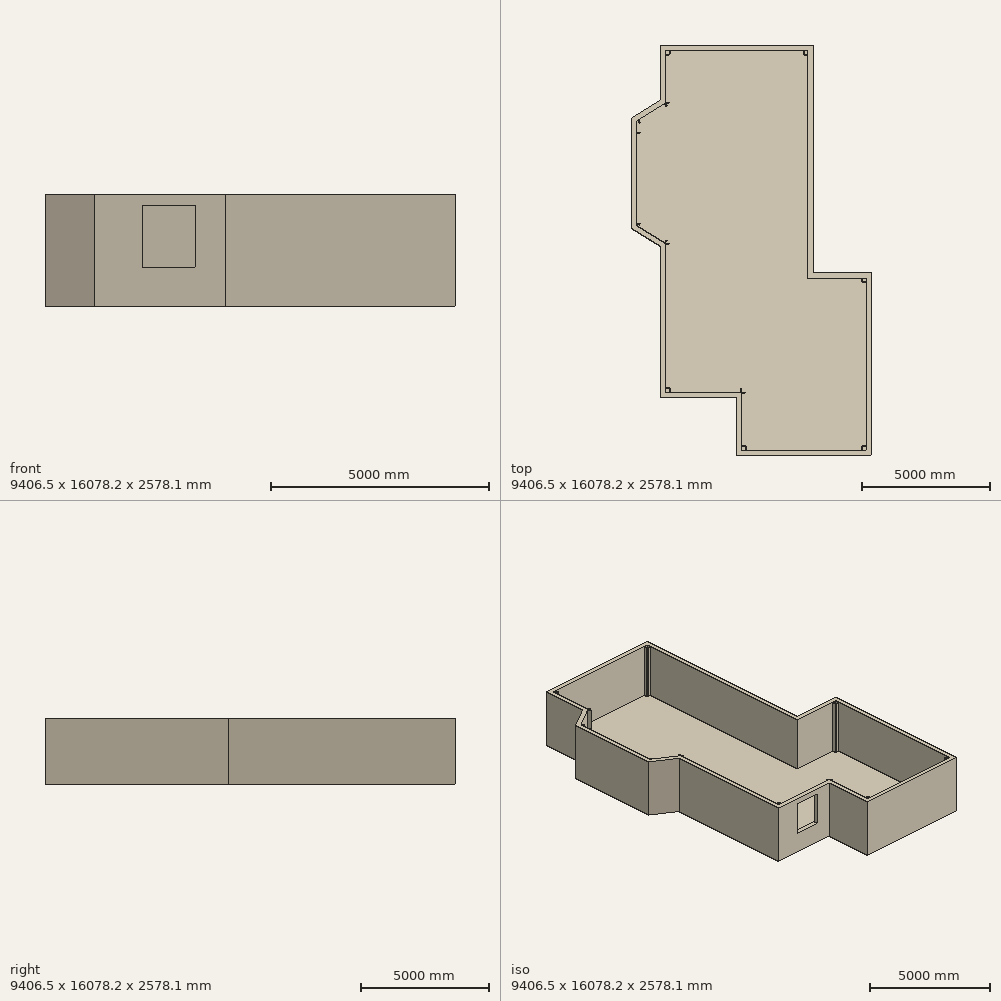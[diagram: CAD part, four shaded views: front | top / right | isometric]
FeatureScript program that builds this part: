
annotation { "Feature Type Name" : "Feature", "Feature Type Description" : "" }
export const myFeature = defineFeature(function(context is Context, id is Id, definition is map)
    precondition{}
    {
        {
            var Q0;
            Q0=qCreatedBy(makeId("Top.planeOp"),FACE);
            var sketch = newSketch(context, id + "F0", { "sketchPlane" : qUnion([Q0])});
            skLineSegment(sketch, "E0", {"start": v(-8280.4, 16078.2) * mm, "end": v(-2286, 16078.2) * mm});
            skLineSegment(sketch, "E1", {"start": v(-2286, 16078.2) * mm, "end": v(-2286, 7162.8) * mm});
            skLineSegment(sketch, "E2", {"start": v(-2286, 7162.8) * mm, "end": v(0, 7162.8) * mm});
            skLineSegment(sketch, "E3", {"start": v(0, 7162.8) * mm, "end": v(0, 0) * mm});
            skLineSegment(sketch, "E4", {"start": v(0, 0) * mm, "end": v(-5283.2, 0) * mm});
            skLineSegment(sketch, "E5", {"start": v(-5283.2, 0) * mm, "end": v(-5283.2, 2286) * mm});
            skLineSegment(sketch, "E6", {"start": v(-5283.2, 2286) * mm, "end": v(-8280.4, 2286) * mm});
            skLineSegment(sketch, "E7", {"start": v(-8280.4, 2286) * mm, "end": v(-8280.4, 8201.03) * mm});
            skLineSegment(sketch, "E8", {"start": v(-8280.4, 8201.03) * mm, "end": v(-9406.5, 8900.32) * mm});
            skLineSegment(sketch, "E9", {"start": v(-9406.5, 8900.32) * mm, "end": v(-9406.5, 13223.08) * mm});
            skLineSegment(sketch, "E10", {"start": v(-9406.5, 13223.08) * mm, "end": v(-8280.4, 13922.38) * mm});
            skLineSegment(sketch, "E11", {"start": v(-8280.4, 13922.38) * mm, "end": v(-8280.4, 16078.2) * mm});
            skSolve(sketch);
        }
        {
            var Q0;
            Q0=qSketchRegion(id+"F0",true);
            extrude(context, id + "F1", {"entities" : qUnion([Q0]), "depth" : 2578.1 * mm});
        }
        {
            var Q0;
            Q0=makeQuery(id+"F1.opExtrude","CAP_FACE",FACE,{"disambiguationData":[OSD([sQuery(id+"F0.wireOp",EDGE,"E0"),sQuery(id+"F0.wireOp",EDGE,"E1"),sQuery(id+"F0.wireOp",EDGE,"E2"),sQuery(id+"F0.wireOp",EDGE,"E3"),sQuery(id+"F0.wireOp",EDGE,"E4"),sQuery(id+"F0.wireOp",EDGE,"E5"),sQuery(id+"F0.wireOp",EDGE,"E6"),sQuery(id+"F0.wireOp",EDGE,"E7"),sQuery(id+"F0.wireOp",EDGE,"E8"),sQuery(id+"F0.wireOp",EDGE,"E9"),sQuery(id+"F0.wireOp",EDGE,"E10"),sQuery(id+"F0.wireOp",EDGE,"E11")])],"isStart":false});
            shell(context, id + "F2", {"entities" : qUnion([Q0]), "thickness" : 203.2 * mm});
        }
        {
            var Q0;
            Q0=makeQuery(id+"F2.opShell","OFFSET_FACE",FACE,{"disambiguationData":[OSD([sQuery(id+"F0.wireOp",EDGE,"E6")])]});
            var sketch = newSketch(context, id + "F3", { "sketchPlane" : qUnion([Q0])});
            skLineSegment(sketch, "E12.bottom", {"start": v(5969, 2324.1) * mm, "end": v(7188.2, 2324.1) * mm});
            skLineSegment(sketch, "E12.top", {"start": v(5969, 901.7) * mm, "end": v(7188.2, 901.7) * mm});
            skLineSegment(sketch, "E12.left", {"start": v(5969, 2324.1) * mm, "end": v(5969, 901.7) * mm});
            skLineSegment(sketch, "E12.right", {"start": v(7188.2, 2324.1) * mm, "end": v(7188.2, 901.7) * mm});
            skPoint(sketch, "E13", {"position": v(6578.6, 2324.1) * mm});
            skSolve(sketch);
        }
        {
            var Q0;
            Q0=makeQuery(id+"F2.opShell","OFFSET_FACE",FACE,{"disambiguationData":[OSD([sQuery(id+"F0.wireOp",EDGE,"E0"),sQuery(id+"F0.wireOp",EDGE,"E1"),sQuery(id+"F0.wireOp",EDGE,"E2"),sQuery(id+"F0.wireOp",EDGE,"E3"),sQuery(id+"F0.wireOp",EDGE,"E4"),sQuery(id+"F0.wireOp",EDGE,"E5"),sQuery(id+"F0.wireOp",EDGE,"E6"),sQuery(id+"F0.wireOp",EDGE,"E7"),sQuery(id+"F0.wireOp",EDGE,"E8"),sQuery(id+"F0.wireOp",EDGE,"E9"),sQuery(id+"F0.wireOp",EDGE,"E10"),sQuery(id+"F0.wireOp",EDGE,"E11")])]});
            var sketch = newSketch(context, id + "F4", { "sketchPlane" : qUnion([Q0])});
            skLineSegment(sketch, "E14.bottom", {"start": v(-8077.2, 13811.9) * mm, "end": v(-7937.5, 13811.9) * mm});
            skLineSegment(sketch, "E14.top", {"start": v(-8077.2, 13850) * mm, "end": v(-7937.5, 13850) * mm});
            skLineSegment(sketch, "E14.left", {"start": v(-8077.2, 13811.9) * mm, "end": v(-8077.2, 13850) * mm});
            skLineSegment(sketch, "E14.right", {"start": v(-7937.5, 13811.9) * mm, "end": v(-7937.5, 13850) * mm});
            skLineSegment(sketch, "E15.bottom", {"start": v(-7934.96, 15875) * mm, "end": v(-7896.86, 15875) * mm});
            skLineSegment(sketch, "E15.top", {"start": v(-7934.96, 15735.3) * mm, "end": v(-7896.86, 15735.3) * mm});
            skLineSegment(sketch, "E15.left", {"start": v(-7934.96, 15875) * mm, "end": v(-7934.96, 15735.3) * mm});
            skLineSegment(sketch, "E15.right", {"start": v(-7896.86, 15875) * mm, "end": v(-7896.86, 15735.3) * mm});
            skLineSegment(sketch, "E16.bottom", {"start": v(-8077.2, 15694.66) * mm, "end": v(-7937.5, 15694.66) * mm});
            skLineSegment(sketch, "E16.top", {"start": v(-8077.2, 15732.76) * mm, "end": v(-7937.5, 15732.76) * mm});
            skLineSegment(sketch, "E16.left", {"start": v(-8077.2, 15694.66) * mm, "end": v(-8077.2, 15732.76) * mm});
            skLineSegment(sketch, "E16.right", {"start": v(-7937.5, 15694.66) * mm, "end": v(-7937.5, 15732.76) * mm});
            skLineSegment(sketch, "E17.bottom", {"start": v(-2631.44, 15875) * mm, "end": v(-2669.54, 15875) * mm});
            skLineSegment(sketch, "E17.top", {"start": v(-2631.44, 15735.3) * mm, "end": v(-2669.54, 15735.3) * mm});
            skLineSegment(sketch, "E17.left", {"start": v(-2631.44, 15875) * mm, "end": v(-2631.44, 15735.3) * mm});
            skLineSegment(sketch, "E17.right", {"start": v(-2669.54, 15875) * mm, "end": v(-2669.54, 15735.3) * mm});
            skLineSegment(sketch, "E18.bottom", {"start": v(-2489.2, 15694.66) * mm, "end": v(-2628.9, 15694.66) * mm});
            skLineSegment(sketch, "E18.top", {"start": v(-2489.2, 15732.76) * mm, "end": v(-2628.9, 15732.76) * mm});
            skLineSegment(sketch, "E18.left", {"start": v(-2489.2, 15694.66) * mm, "end": v(-2489.2, 15732.76) * mm});
            skLineSegment(sketch, "E18.right", {"start": v(-2628.9, 15694.66) * mm, "end": v(-2628.9, 15732.76) * mm});
            skLineSegment(sketch, "E19", {"start": v(-8078.22, 13808.73) * mm, "end": v(-8110.59, 13788.64) * mm});
            skLineSegment(sketch, "E20", {"start": v(-8110.59, 13788.64) * mm, "end": v(-8036.89, 13669.96) * mm});
            skLineSegment(sketch, "E21", {"start": v(-8036.89, 13669.96) * mm, "end": v(-8004.52, 13690.06) * mm});
            skLineSegment(sketch, "E22", {"start": v(-8004.52, 13690.06) * mm, "end": v(-8078.22, 13808.73) * mm});
            skLineSegment(sketch, "E23.bottom", {"start": v(-9203.3, 12669.47) * mm, "end": v(-9063.6, 12669.47) * mm});
            skLineSegment(sketch, "E23.top", {"start": v(-9203.3, 12631.37) * mm, "end": v(-9063.6, 12631.37) * mm});
            skLineSegment(sketch, "E23.left", {"start": v(-9203.3, 12669.47) * mm, "end": v(-9203.3, 12631.37) * mm});
            skLineSegment(sketch, "E23.right", {"start": v(-9063.6, 12669.47) * mm, "end": v(-9063.6, 12631.37) * mm});
            skLineSegment(sketch, "E24", {"start": v(-9162.3, 13135.53) * mm, "end": v(-9129.94, 13155.63) * mm});
            skLineSegment(sketch, "E25", {"start": v(-9129.94, 13155.63) * mm, "end": v(-9056.24, 13036.95) * mm});
            skLineSegment(sketch, "E26", {"start": v(-9056.24, 13036.95) * mm, "end": v(-9088.6, 13016.85) * mm});
            skLineSegment(sketch, "E27", {"start": v(-9088.6, 13016.85) * mm, "end": v(-9162.3, 13135.53) * mm});
            skLineSegment(sketch, "E28", {"start": v(-9162.3, 8987.87) * mm, "end": v(-9088.6, 9106.55) * mm});
            skLineSegment(sketch, "E29", {"start": v(-9088.6, 9106.55) * mm, "end": v(-9056.24, 9086.45) * mm});
            skLineSegment(sketch, "E30", {"start": v(-9056.24, 9086.45) * mm, "end": v(-9129.94, 8967.77) * mm});
            skLineSegment(sketch, "E31", {"start": v(-9129.94, 8967.77) * mm, "end": v(-9162.3, 8987.87) * mm});
            skLineSegment(sketch, "E32", {"start": v(-8109.57, 8334.13) * mm, "end": v(-8077.2, 8314.03) * mm});
            skLineSegment(sketch, "E33", {"start": v(-8077.2, 8314.03) * mm, "end": v(-8003.5, 8432.71) * mm});
            skLineSegment(sketch, "E34", {"start": v(-8003.5, 8432.71) * mm, "end": v(-8035.87, 8452.81) * mm});
            skLineSegment(sketch, "E35", {"start": v(-8035.87, 8452.81) * mm, "end": v(-8109.57, 8334.13) * mm});
            skLineSegment(sketch, "E36.bottom", {"start": v(-9203.3, 9061.59) * mm, "end": v(-9063.6, 9061.59) * mm});
            skLineSegment(sketch, "E36.top", {"start": v(-9203.3, 9099.69) * mm, "end": v(-9063.6, 9099.69) * mm});
            skLineSegment(sketch, "E36.left", {"start": v(-9203.3, 9061.59) * mm, "end": v(-9203.3, 9099.69) * mm});
            skLineSegment(sketch, "E36.right", {"start": v(-9063.6, 9061.59) * mm, "end": v(-9063.6, 9099.69) * mm});
            skLineSegment(sketch, "E37.bottom", {"start": v(-8077.2, 8311.5) * mm, "end": v(-7937.5, 8311.5) * mm});
            skLineSegment(sketch, "E37.top", {"start": v(-8077.2, 8273.4) * mm, "end": v(-7937.5, 8273.4) * mm});
            skLineSegment(sketch, "E37.left", {"start": v(-8077.2, 8311.5) * mm, "end": v(-8077.2, 8273.4) * mm});
            skLineSegment(sketch, "E37.right", {"start": v(-7937.5, 8311.5) * mm, "end": v(-7937.5, 8273.4) * mm});
            skLineSegment(sketch, "E38.bottom", {"start": v(-8077.2, 2631.44) * mm, "end": v(-7937.5, 2631.44) * mm});
            skLineSegment(sketch, "E38.top", {"start": v(-8077.2, 2669.54) * mm, "end": v(-7937.5, 2669.54) * mm});
            skLineSegment(sketch, "E38.left", {"start": v(-8077.2, 2631.44) * mm, "end": v(-8077.2, 2669.54) * mm});
            skLineSegment(sketch, "E38.right", {"start": v(-7937.5, 2631.44) * mm, "end": v(-7937.5, 2669.54) * mm});
            skLineSegment(sketch, "E39.bottom", {"start": v(-7896.86, 2489.2) * mm, "end": v(-7934.96, 2489.2) * mm});
            skLineSegment(sketch, "E39.top", {"start": v(-7896.86, 2628.9) * mm, "end": v(-7934.96, 2628.9) * mm});
            skLineSegment(sketch, "E39.left", {"start": v(-7896.86, 2489.2) * mm, "end": v(-7896.86, 2628.9) * mm});
            skLineSegment(sketch, "E39.right", {"start": v(-7934.96, 2489.2) * mm, "end": v(-7934.96, 2628.9) * mm});
            skLineSegment(sketch, "E40.bottom", {"start": v(-5082.54, 2489.2) * mm, "end": v(-5120.64, 2489.2) * mm});
            skLineSegment(sketch, "E40.top", {"start": v(-5082.54, 2628.9) * mm, "end": v(-5120.64, 2628.9) * mm});
            skLineSegment(sketch, "E40.left", {"start": v(-5082.54, 2489.2) * mm, "end": v(-5082.54, 2628.9) * mm});
            skLineSegment(sketch, "E40.right", {"start": v(-5120.64, 2489.2) * mm, "end": v(-5120.64, 2628.9) * mm});
            skLineSegment(sketch, "E41.top", {"start": v(-5080, 2448.56) * mm, "end": v(-4940.3, 2448.56) * mm});
            skLineSegment(sketch, "E41.right", {"start": v(-4940.3, 2486.66) * mm, "end": v(-4940.3, 2448.56) * mm});
            skLineSegment(sketch, "E42.bottom", {"start": v(-5080, 345.44) * mm, "end": v(-4940.3, 345.44) * mm});
            skLineSegment(sketch, "E42.top", {"start": v(-5080, 383.54) * mm, "end": v(-4940.3, 383.54) * mm});
            skLineSegment(sketch, "E42.left", {"start": v(-5080, 345.44) * mm, "end": v(-5080, 383.54) * mm});
            skLineSegment(sketch, "E42.right", {"start": v(-4940.3, 345.44) * mm, "end": v(-4940.3, 383.54) * mm});
            skLineSegment(sketch, "E43.bottom", {"start": v(-4937.76, 203.2) * mm, "end": v(-4899.66, 203.2) * mm});
            skLineSegment(sketch, "E43.top", {"start": v(-4937.76, 342.9) * mm, "end": v(-4899.66, 342.9) * mm});
            skLineSegment(sketch, "E43.left", {"start": v(-4937.76, 203.2) * mm, "end": v(-4937.76, 342.9) * mm});
            skLineSegment(sketch, "E43.right", {"start": v(-4899.66, 203.2) * mm, "end": v(-4899.66, 342.9) * mm});
            skLineSegment(sketch, "E44.bottom", {"start": v(-383.54, 203.2) * mm, "end": v(-345.44, 203.2) * mm});
            skLineSegment(sketch, "E44.top", {"start": v(-383.54, 342.9) * mm, "end": v(-345.44, 342.9) * mm});
            skLineSegment(sketch, "E44.left", {"start": v(-383.54, 203.2) * mm, "end": v(-383.54, 342.9) * mm});
            skLineSegment(sketch, "E44.right", {"start": v(-345.44, 203.2) * mm, "end": v(-345.44, 342.9) * mm});
            skLineSegment(sketch, "E45.bottom", {"start": v(-203.2, 345.44) * mm, "end": v(-342.9, 345.44) * mm});
            skLineSegment(sketch, "E45.top", {"start": v(-203.2, 383.54) * mm, "end": v(-342.9, 383.54) * mm});
            skLineSegment(sketch, "E45.left", {"start": v(-203.2, 345.44) * mm, "end": v(-203.2, 383.54) * mm});
            skLineSegment(sketch, "E45.right", {"start": v(-342.9, 345.44) * mm, "end": v(-342.9, 383.54) * mm});
            skLineSegment(sketch, "E46.bottom", {"start": v(-203.2, 6779.26) * mm, "end": v(-342.9, 6779.26) * mm});
            skLineSegment(sketch, "E46.top", {"start": v(-203.2, 6817.36) * mm, "end": v(-342.9, 6817.36) * mm});
            skLineSegment(sketch, "E46.left", {"start": v(-203.2, 6779.26) * mm, "end": v(-203.2, 6817.36) * mm});
            skLineSegment(sketch, "E46.right", {"start": v(-342.9, 6779.26) * mm, "end": v(-342.9, 6817.36) * mm});
            skLineSegment(sketch, "E47.bottom", {"start": v(-345.44, 6959.6) * mm, "end": v(-383.54, 6959.6) * mm});
            skLineSegment(sketch, "E47.top", {"start": v(-345.44, 6819.9) * mm, "end": v(-383.54, 6819.9) * mm});
            skLineSegment(sketch, "E47.left", {"start": v(-345.44, 6959.6) * mm, "end": v(-345.44, 6819.9) * mm});
            skLineSegment(sketch, "E47.right", {"start": v(-383.54, 6959.6) * mm, "end": v(-383.54, 6819.9) * mm});
            skLineSegment(sketch, "E48", {"start": v(-4940.3, 2486.66) * mm, "end": v(-5080, 2486.66) * mm});
            skLineSegment(sketch, "E49", {"start": v(-5080, 2486.66) * mm, "end": v(-5080, 2448.56) * mm});
            skLineSegment(sketch, "E50", {"start": v(-9203.3, 13110.07) * mm, "end": v(-9045.7, 12987.43) * mm, "construction": true});
            skLineSegment(sketch, "E51", {"start": v(-9045.7, 12987.43) * mm, "end": v(-9104.83, 13171.22) * mm, "construction": true});
            skLineSegment(sketch, "E52", {"start": v(-9104.83, 13171.22) * mm, "end": v(-9203.3, 12968.55) * mm, "construction": true});
            skLineSegment(sketch, "E53", {"start": v(-9203.3, 12968.55) * mm, "end": v(-9045.7, 12987.43) * mm, "construction": true});
            skSolve(sketch);
        }
        {
            var Q0;
            Q0=qSketchRegion(id+"F3",true);
            var Q1;
            Q1=makeQuery(id+"F8.opExtrude","SWEPT_FACE",FACE,{"disambiguationData":[OSD([sQuery(id+"FoojXG4nMktDod7_1.wireOp",EDGE,"1VciS72g-VBcj-X035-P1CE-B9HJ2LFSvZOH.top"),sQuery(id+"FoojXG4nMktDod7_1.wireOp",EDGE,"icQnHHDd-8pVd-SaWu-tjJm-3fqmfHu7QenC")])]});
            extrude(context, id + "F5", {"entities" : qUnion([Q0]), "operationType" : NewBodyOperationType.REMOVE, "endBound" : BoundingType.UP_TO_NEXT, "oppositeDirection" : true, "depth" : 25.4 * mm});
        }
        {
            var Q0;
            Q0 = qSketchRegion(id + "F4", true);
            extrude(context, id + "F6", {"entities" : qUnion([Q0]), "depth" : 2349.5 * mm});
        }
        {
            var Q0;
            Q0=qSketchRegion(id+"F4",true);
            extrude(context, id + "F7", {"entities" : qUnion([Q0]), "operationType" : NewBodyOperationType.ADD, "depth" : 2349.5 * mm});
        }
    });
